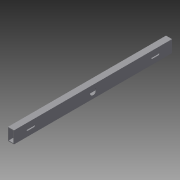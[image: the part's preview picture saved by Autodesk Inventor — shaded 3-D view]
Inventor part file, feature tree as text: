
AUTODESK INVENTOR PART (.ipt)
format: ipt  version: 2015 SP1 (Build 190203100, 203)  size: 124,416 bytes
history: native  units: in
note: dims shown in document units (in); Inventor stores cm internally (conversion verified against a paired STEP export)
features: extrude x2, sketch x2, projected_geometry x1
ambient origin geometry x8: Origin, YZ Plane, XZ Plane, XY Plane, X Axis, Y Axis, Z Axis, Center Point
bodies: Solid1 (feature_tree)
feature tree (5):
  extrude  "Extrusion1"  Depth=2.0in
  extrude  "Extrusion2"  Depth=1.75in
  sketch  "Sketch1"  dims[d0=1.0in d1=2.0in]
  sketch  "Sketch2"  dims[d2=0.75in d3=1.75in d4=0.125in d5=0.125in d6=26.0in d7=0.0in d8=1.0in d9=13.0in d10=1.0in d11=1.0in d12=1.0in d13=1.0in d14=1.0in d15=2.25in d16=2.25in d17=3.25in d18=3.25in d19=0.1875in d20=0.375in d21=0.1875in d22=0.375in d23=0.1875in d24=90.0deg d25=0.375in d26=0.1875in d27=90.0deg d28=0.375in d29=0.1877in d30=0.1892in d31=0.1901in d32=0.1875in d33=30.0in d34=0.0in]
  projected_geometry  "Projected Loop1"
